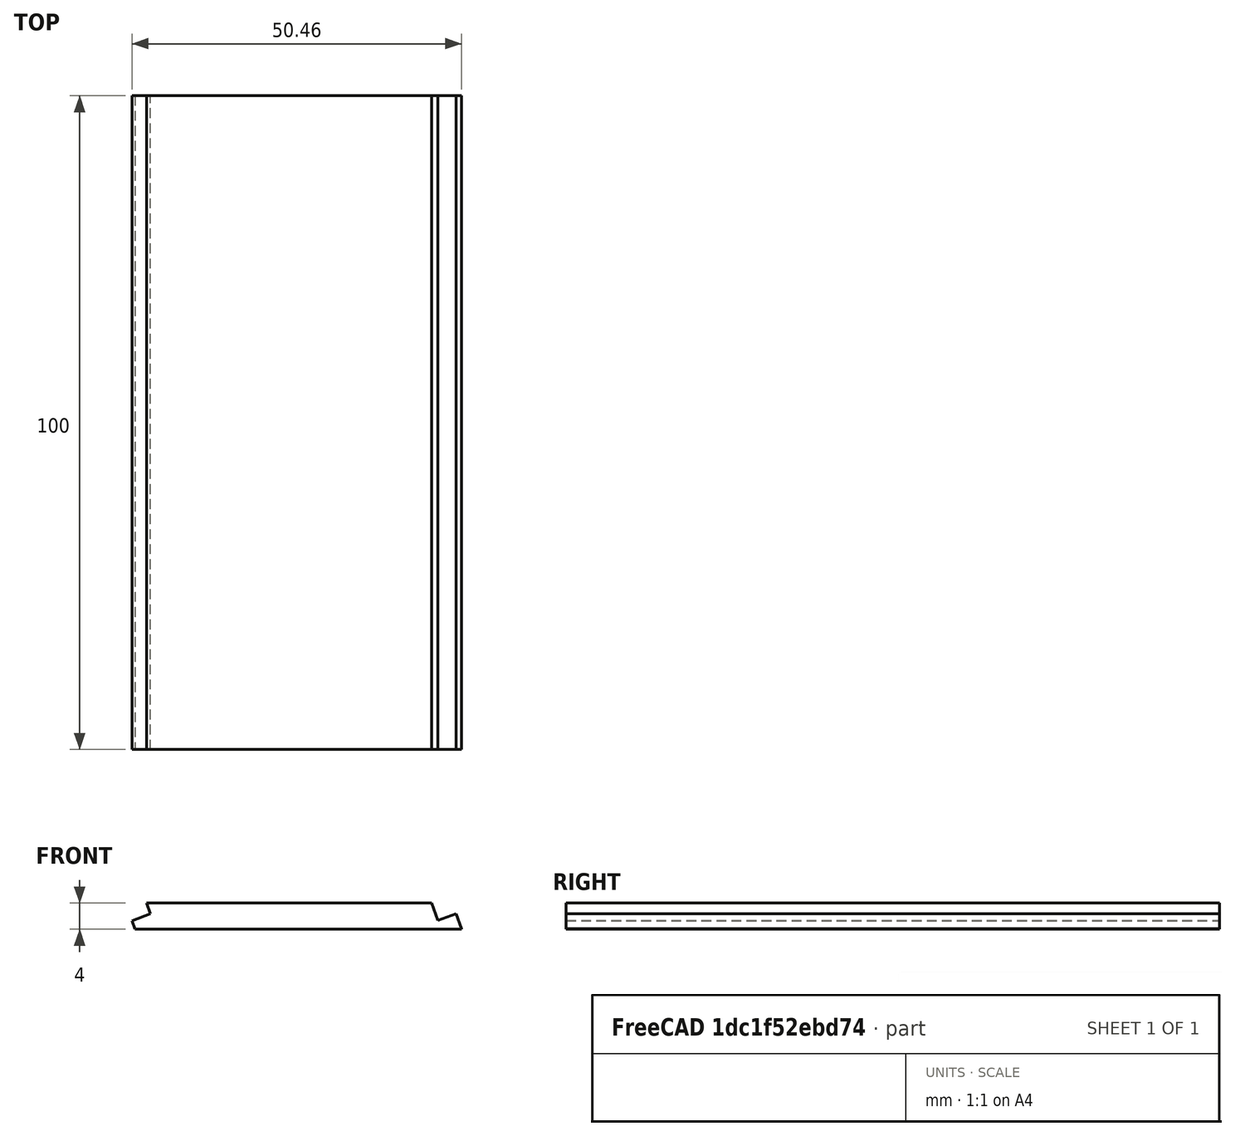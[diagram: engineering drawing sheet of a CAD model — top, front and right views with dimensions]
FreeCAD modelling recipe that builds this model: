
FCSTD DOCUMENT  (FreeCAD 0.16R6706 (Git))
Label: tapa alante tumbada
License: All rights reserved
LicenseURL: http://en.wikipedia.org/wiki/All_rights_reserved
objects: Part::Box×5, Part::Cut×4
note: 9 computed .brp shape members not serialized (recipe doc carries the construction recipe); baked Part::Feature solids carry a one-line shape summary decoded from their .brp

FEATURE [Part::Box] Box014  label="rampa"
  Height = 51
  Length = 4
  Placement = pos=(-2.4997,0,0.0349048) rot=(0,1,0;0.349066rad)
  Width = 100
FEATURE [Part::Box] Box015  label="plancha resta abajo"
  Height = 3
  Length = 27
  Placement = pos=(-9,0,-3) rot=(0,0,1;0rad)
  Width = 100
FEATURE [Part::Box] Box016  label="plancha resta arriba"
  Height = 3
  Length = 27
  Placement = pos=(5,0,47) rot=(0,0,1;0rad)
  Width = 100
FEATURE [Part::Cut] Cut009
  Base = -> Box014
  Tool = -> Box015
FEATURE [Part::Cut] Cut010  label="tapa alante"
  Base = -> Cut009
  Tool = -> Box016
FEATURE [Part::Box] Box017  label="ranura inferiror"
  Height = 3
  Length = 15
  Width = 100
FEATURE [Part::Box] Box018  label="ranura superior"
  Height = 3
  Length = 15
  Placement = pos=(16,0,44) rot=(0,0,1;0rad)
  Width = 100
FEATURE [Part::Cut] Cut011
  Base = -> Cut010
  Tool = -> Box017
FEATURE [Part::Cut] Cut012  label="tapa alante con ranuras"
  Base = -> Cut011
  Placement = pos=(0,0,3) rot=(0,-1,0;1.91986rad)
  Tool = -> Box018
